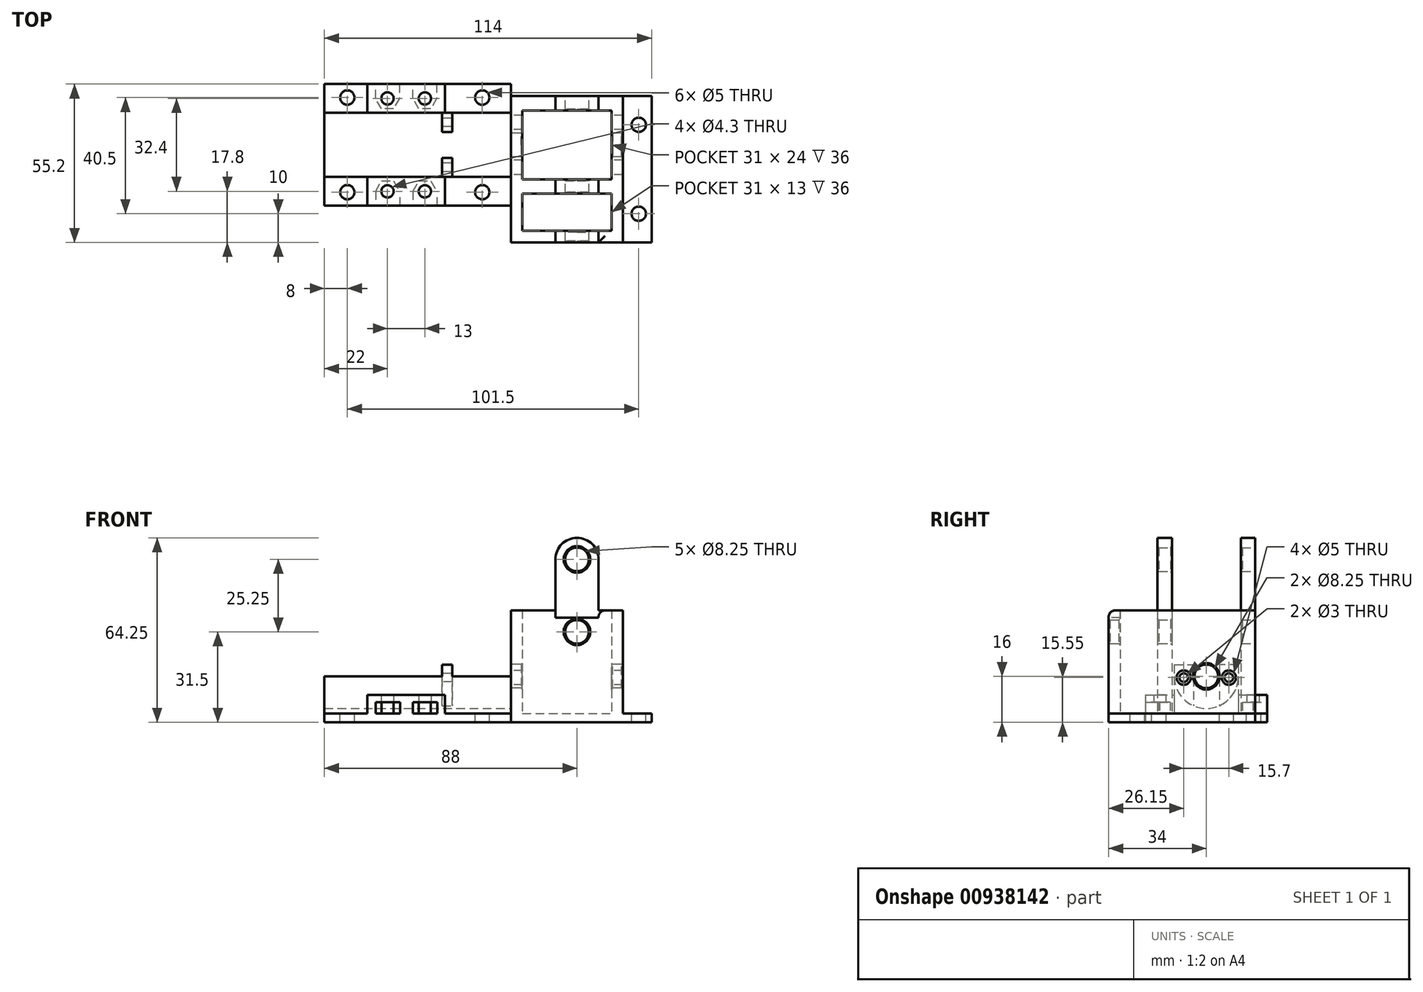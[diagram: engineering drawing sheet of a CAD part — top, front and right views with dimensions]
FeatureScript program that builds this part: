
annotation { "Feature Type Name" : "Feature", "Feature Type Description" : "" }
export const myFeature = defineFeature(function(context is Context, id is Id, definition is map)
    precondition{}
    {
        {
            var Q0;
            Q0=qCreatedBy(makeId("Top.planeOp"),FACE);
            var sketch = newSketch(context, id + "F0", { "sketchPlane" : qUnion([Q0])});
            skPoint(sketch, "E0.middle", {"position": v(0, 0) * mm});
            skLineSegment(sketch, "E1", {"start": v(0, 25.5) * mm, "end": v(0, -25.5) * mm});
            skLineSegment(sketch, "E2.bottom", {"start": v(0, 25.5) * mm, "end": v(39, 25.5) * mm});
            skLineSegment(sketch, "E2.right", {"start": v(39, 25.5) * mm, "end": v(39, -25.5) * mm});
            skLineSegment(sketch, "E3", {"start": v(4, 20.5) * mm, "end": v(35, 20.5) * mm});
            skLineSegment(sketch, "E4", {"start": v(0, -25.5) * mm, "end": v(39, -25.5) * mm});
            skLineSegment(sketch, "E5", {"start": v(4, 20.5) * mm, "end": v(4, -3.5) * mm});
            skLineSegment(sketch, "E6", {"start": v(35, 20.5) * mm, "end": v(35, -3.5) * mm});
            skLineSegment(sketch, "E7", {"start": v(35, -21.5) * mm, "end": v(4, -21.5) * mm});
            skLineSegment(sketch, "E8", {"start": v(23, 20.5) * mm, "end": v(23, -21.5) * mm, "construction": true});
            skLineSegment(sketch, "E9", {"start": v(4, -3.5) * mm, "end": v(35, -3.5) * mm});
            skLineSegment(sketch, "E10", {"start": v(4, -8.5) * mm, "end": v(35, -8.5) * mm});
            skLineSegment(sketch, "E11", {"start": v(35, -8.5) * mm, "end": v(35, -21.5) * mm});
            skLineSegment(sketch, "E12", {"start": v(4, -8.5) * mm, "end": v(4, -21.5) * mm});
            skLineSegment(sketch, "E13", {"start": v(39, 25.5) * mm, "end": v(49, 25.5) * mm});
            skLineSegment(sketch, "E14", {"start": v(49, 25.5) * mm, "end": v(49, -25.5) * mm});
            skLineSegment(sketch, "E15", {"start": v(49, -25.5) * mm, "end": v(39, -25.5) * mm});
            skCircle(sketch, "E16", {"center": v(44.5, 15.5) * mm, "radius": 2.5 * mm});
            skCircle(sketch, "E17", {"center": v(44.5, -15.5) * mm, "radius": 2.5 * mm});
            skLineSegment(sketch, "E18", {"start": v(44.5, 15.5) * mm, "end": v(44.5, -15.5) * mm, "construction": true});
            skPoint(sketch, "E19", {"position": v(44.5, 0) * mm});
            skPoint(sketch, "E20", {"position": v(49, 0) * mm});
            skSolve(sketch);
        }
        {
            var Q0;
            Q0=makeQuery(id+"F0.imprint","IMPRINT",FACE,{"disambiguationData":[TD([[makeQuery(id+"F0.imprint","IMPRINT",EDGE,{"derivedFrom":sQuery(id+"F0.wireOp",EDGE,"E3")}),-1.0]])]});
            var Q1;
            Q1=makeQuery(id+"F0.imprint","IMPRINT",FACE,{"disambiguationData":[TD([[makeQuery(id+"F0.imprint","IMPRINT",EDGE,{"derivedFrom":sQuery(id+"F0.wireOp",EDGE,"E7")}),-1.0]])]});
            var Q2;
            Q2=makeQuery(id+"F0.imprint","IMPRINT",FACE,{"disambiguationData":[TD([[makeQuery(id+"F0.imprint","IMPRINT",EDGE,{"derivedFrom":sQuery(id+"F0.wireOp",EDGE,"E2.right")}),1.0]])]});
            var Q3;
            Q3=makeQuery(id+"F0.imprint","IMPRINT",FACE,{"disambiguationData":[TD([[makeQuery(id+"F0.imprint","IMPRINT",EDGE,{"derivedFrom":sQuery(id+"F0.wireOp",EDGE,"E1")}),1.0]])]});
            extrude(context, id + "F1", {"entities" : qUnion([Q0, Q1, Q2, Q3]), "oppositeDirection" : true, "depth" : 3 * mm, "offsetDistance" : 25 * mm});
        }
        {
            var Q0;
            {var subQ0=sQuery(id+"F0.wireOp",EDGE,"E1");Q0=makeQuery(id+"F0.imprint","IMPRINT",FACE,{"disambiguationData":[TD([[makeQuery(id+"F0.imprint","IMPRINT",EDGE,{"derivedFrom":subQ0}),1.0]])]});}
            extrude(context, id + "F2", {"entities" : qUnion([Q0]), "operationType" : NewBodyOperationType.ADD, "depth" : 13 * mm + 15.5 * mm + 7.5 * mm, "offsetDistance" : 25 * mm});
        }
        {
            var Q0;
            Q0=makeQuery(id+"F2.opExtrude","SWEPT_FACE",FACE,{"disambiguationData":[OSD([sQuery(id+"F0.wireOp",EDGE,"E1")])]});
            var sketch = newSketch(context, id + "F3", { "sketchPlane" : qUnion([Q0])});
            skCircle(sketch, "E21", {"center": v(-8.5, 13) * mm, "radius": 4.12 * mm});
            skLineSegment(sketch, "E22", {"start": v(-19.7, -3) * mm, "end": v(2.7, -3) * mm});
            skArc(sketch, "E23", {"start": v(-19.7, 13) * mm, "mid": v(-8.5, 1.8) * mm, "end": v(2.7, 13) * mm});
            skLineSegment(sketch, "E24", {"start": v(-19.7, 13) * mm, "end": v(-19.7, -3) * mm});
            skLineSegment(sketch, "E25", {"start": v(2.7, 13) * mm, "end": v(2.7, -3) * mm});
            skPoint(sketch, "E26.orphan", {"position": v(-8.25, 36) * mm});
            skLineSegment(sketch, "E27", {"start": v(-8.5, 13) * mm, "end": v(-8.5, 22.2) * mm, "construction": true});
            skLineSegment(sketch, "E28", {"start": v(2.7, 0) * mm, "end": v(12.7, 0) * mm});
            skLineSegment(sketch, "E29", {"start": v(12.7, 0) * mm, "end": v(12.7, -3) * mm});
            skLineSegment(sketch, "E30", {"start": v(12.7, -3) * mm, "end": v(2.7, -3) * mm});
            skLineSegment(sketch, "E31", {"start": v(-19.7, 0) * mm, "end": v(-29.7, 0) * mm});
            skLineSegment(sketch, "E32", {"start": v(-29.7, 0) * mm, "end": v(-29.7, -3) * mm});
            skLineSegment(sketch, "E33", {"start": v(-29.7, -3) * mm, "end": v(-19.7, -3) * mm});
            skSolve(sketch);
        }
        {
            var Q0;
            Q0=makeQuery(id+"F3.imprint","IMPRINT",FACE,{"disambiguationData":[TD([[makeQuery(id+"F3.imprint","IMPRINT",EDGE,{"derivedFrom":sQuery(id+"F3.wireOp",EDGE,"E21")}),1.0]])]});
            extrude(context, id + "F4", {"entities" : qUnion([Q0]), "operationType" : NewBodyOperationType.REMOVE, "endBound" : BoundingType.THROUGH_ALL, "oppositeDirection" : true, "depth" : 3 * mm, "offsetDistance" : 25 * mm});
        }
        {
            var Q0;
            Q0=makeQuery(id+"F2.opExtrude","CAP_FACE",FACE,{"disambiguationData":[OSD([sQuery(id+"F0.wireOp",EDGE,"E1"),sQuery(id+"F0.wireOp",EDGE,"E2.bottom"),sQuery(id+"F0.wireOp",EDGE,"E2.top"),sQuery(id+"F0.wireOp",EDGE,"E2.right"),sQuery(id+"F0.wireOp",EDGE,"gcLeu1ae-8P9o-23Q4-LKgT-iucjTtS8KbHA"),sQuery(id+"F0.wireOp",EDGE,"E3"),sQuery(id+"F0.wireOp",EDGE,"sOh78GjP-uAya-5xBB-zDQr-sfzLusMJ1pns")])],"isStart":false});
            var sketch = newSketch(context, id + "F5", { "sketchPlane" : qUnion([Q0])});
            skLineSegment(sketch, "E34.bottom", {"start": v(30.5, 20.5) * mm, "end": v(15.5, 20.5) * mm});
            skLineSegment(sketch, "E34.top", {"start": v(30.5, 25.5) * mm, "end": v(15.5, 25.5) * mm});
            skLineSegment(sketch, "E34.left", {"start": v(30.5, 20.5) * mm, "end": v(30.5, 25.5) * mm});
            skLineSegment(sketch, "E34.right", {"start": v(15.5, 20.5) * mm, "end": v(15.5, 25.5) * mm});
            skPoint(sketch, "E35", {"position": v(23, 20.5) * mm});
            skLineSegment(sketch, "E36.bottom", {"start": v(15.5, -3.5) * mm, "end": v(30.5, -3.5) * mm});
            skLineSegment(sketch, "E36.top", {"start": v(15.5, -8.5) * mm, "end": v(30.5, -8.5) * mm});
            skLineSegment(sketch, "E36.left", {"start": v(15.5, -3.5) * mm, "end": v(15.5, -8.5) * mm});
            skLineSegment(sketch, "E36.right", {"start": v(30.5, -3.5) * mm, "end": v(30.5, -8.5) * mm});
            skLineSegment(sketch, "E37.bottom", {"start": v(30.5, -21.5) * mm, "end": v(15.5, -21.5) * mm});
            skLineSegment(sketch, "E37.top", {"start": v(30.5, -25.5) * mm, "end": v(15.5, -25.5) * mm});
            skLineSegment(sketch, "E37.left", {"start": v(15.5, -21.5) * mm, "end": v(15.5, -25.5) * mm});
            skLineSegment(sketch, "E37.right", {"start": v(30.5, -21.5) * mm, "end": v(30.5, -25.5) * mm});
            skSolve(sketch);
        }
        {
            var Q0;
            Q0=makeQuery(id+"F5.imprint","IMPRINT",FACE,{"disambiguationData":[TD([[makeQuery(id+"F5.imprint","IMPRINT",EDGE,{"derivedFrom":sQuery(id+"F5.wireOp",EDGE,"E34.bottom")}),1.0]])]});
            var Q1;
            Q1=makeQuery(id+"F5.imprint","IMPRINT",FACE,{"disambiguationData":[TD([[makeQuery(id+"F5.imprint","IMPRINT",EDGE,{"derivedFrom":sQuery(id+"F5.wireOp",EDGE,"MIDvq16X-2qJM-DpOX-ttxi-7ILKl5nktbrk.bottom")}),1.0]])]});
            var Q2;
            {var subQ0=sQuery(id+"F5.wireOp",EDGE,"MIDvq16X-2qJM-DpOX-ttxi-7ILKl5nktbrk.top");Q2=makeQuery(id+"F5.imprint","IMPRINT",FACE,{"disambiguationData":[TD([[makeQuery(id+"F5.imprint","IMPRINT",EDGE,{"derivedFrom":subQ0}),1.0]])]});}
            var Q3;
            Q3=makeQuery(id+"F5.imprint","IMPRINT",FACE,{"disambiguationData":[TD([[makeQuery(id+"F5.imprint","IMPRINT",EDGE,{"derivedFrom":sQuery(id+"F5.wireOp",EDGE,"E36.bottom")}),-1.0]])]});
            extrude(context, id + "F6", {"entities" : qUnion([Q0, Q1, Q2, Q3]), "operationType" : NewBodyOperationType.ADD, "depth" : 25.25 * mm, "offsetDistance" : 25 * mm});
        }
        {
            var Q0;
            {var subQ0=sQuery(id+"F0.wireOp",EDGE,"E2.bottom");Q0=makeQuery(id+"F6.boolean.opBoolean","MERGE",FACE,{"derivedFrom":[makeQuery(id+"F2.boolean.opBoolean","MERGE",FACE,{"derivedFrom":[makeQuery(id+"F1.opExtrude","SWEPT_FACE",FACE,{"disambiguationData":[OSD([subQ0])]}),makeQuery(id+"F2.opExtrude","SWEPT_FACE",FACE,{"disambiguationData":[OSD([subQ0])]})]}),makeQuery(id+"F6.opExtrude","SWEPT_FACE",FACE,{"disambiguationData":[OSD([sQuery(id+"F5.wireOp",EDGE,"hZvgbcKE-K8w2-tHia-kABx-2Idw38wRMYFB.top")])]})]});}
            var sketch = newSketch(context, id + "F7", { "sketchPlane" : qUnion([Q0])});
            skCircle(sketch, "E38", {"center": v(-23, 28.5) * mm, "radius": 4.12 * mm});
            skCircle(sketch, "E39", {"center": v(-23, 53.75) * mm, "radius": 4.12 * mm});
            skSolve(sketch);
        }
        {
            var Q0;
            {var subQ0=sQuery(id+"F7.wireOp",EDGE,"E38");var subQ1=sQuery(id+"F5.wireOp",EDGE,"sYnbmEzX-ozCD-b1SQ-Veyi-UDucfDWyLtHq.right");var subQ2=sQuery(id+"F5.wireOp",EDGE,"sYnbmEzX-ozCD-b1SQ-Veyi-UDucfDWyLtHq.bottom");var subQ3=sQuery(id+"F0.wireOp",EDGE,"E2.bottom");var subQ4=makeQuery(id+"FMjW4kx9HAlJB9q_1.opExtrude","SWEPT_EDGE",EDGE,{"disambiguationData":[OSD([subQ3,subQ2,subQ1])]});var subQ5=makeQuery(id+"F7.imprint","INTERSECT",VERTEX,{"derivedFrom":[subQ4,subQ0]});Q0=makeQuery(id+"F7.imprint","IMPRINT",FACE,{"disambiguationData":[TD([[makeQuery(id+"F7.imprint","IMPRINT",EDGE,{"disambiguationData":[TD([[subQ5,1.0]])],"derivedFrom":subQ0}),1.0]])]});}
            var Q1;
            Q1=makeQuery(id+"F7.imprint","IMPRINT",FACE,{"disambiguationData":[TD([[makeQuery(id+"F7.imprint","IMPRINT",EDGE,{"derivedFrom":sQuery(id+"F7.wireOp",EDGE,"E39")}),1.0]])]});
            extrude(context, id + "F8", {"entities" : qUnion([Q0, Q1]), "operationType" : NewBodyOperationType.REMOVE, "endBound" : BoundingType.THROUGH_ALL, "oppositeDirection" : true, "depth" : 25 * mm, "offsetDistance" : 25 * mm});
        }
        {
            var Q0;
            Q0=makeQuery(id+"F3.imprint","IMPRINT",FACE,{"disambiguationData":[TD([[makeQuery(id+"F3.imprint","IMPRINT",EDGE,{"derivedFrom":sQuery(id+"F3.wireOp",EDGE,"E22")}),1.0]])]});
            var Q1;
            {var subQ2=sQuery(id+"F3.wireOp",EDGE,"E28");Q1=makeQuery(id+"F3.imprint","IMPRINT",FACE,{"disambiguationData":[TD([[makeQuery(id+"F3.imprint","IMPRINT",EDGE,{"derivedFrom":subQ2}),-1.0]])]});}
            var Q2;
            {var subQ1=sQuery(id+"F3.wireOp",EDGE,"E24");var subQ3=sQuery(id+"F3.wireOp",EDGE,"E31");var subQ4=makeQuery(id+"F3.imprint","INTERSECT",VERTEX,{"derivedFrom":[subQ1,subQ3]});Q2=makeQuery(id+"F3.imprint","IMPRINT",FACE,{"disambiguationData":[TD([[makeQuery(id+"F3.imprint","IMPRINT",EDGE,{"disambiguationData":[TD([[subQ4,-1.0]])],"derivedFrom":subQ1}),-1.0]])]});}
            var Q3;
            {var subQ0=sQuery(id+"F3.wireOp",EDGE,"E32");Q3=makeQuery(id+"F3.imprint","IMPRINT",FACE,{"disambiguationData":[TD([[makeQuery(id+"F3.imprint","IMPRINT",EDGE,{"derivedFrom":subQ0}),1.0]])]});}
            extrude(context, id + "F9", {"entities" : qUnion([Q0, Q1, Q2, Q3]), "operationType" : NewBodyOperationType.ADD, "depth" : 65 * mm, "offsetDistance" : 25 * mm});
        }
        {
            var Q0;
            Q0=makeQuery(id+"F9.boolean.opBoolean","MERGE",FACE,{"derivedFrom":[makeQuery(id+"F1.opExtrude","CAP_FACE",FACE,{"disambiguationData":[OSD([sQuery(id+"F0.wireOp",EDGE,"E1"),sQuery(id+"F0.wireOp",EDGE,"E2.bottom"),sQuery(id+"F0.wireOp",EDGE,"E2.right"),sQuery(id+"F0.wireOp",EDGE,"E4")])],"isStart":false}),makeQuery(id+"F9.opExtrude","SWEPT_FACE",FACE,{"disambiguationData":[OSD([sQuery(id+"F3.wireOp",EDGE,"E22")])]})]});
            var sketch = newSketch(context, id + "F10", { "sketchPlane" : qUnion([Q0])});
            skLineSegment(sketch, "E40.bottom", {"start": v(-24, 2.7) * mm, "end": v(-20.5, 2.7) * mm});
            skLineSegment(sketch, "E40.top", {"start": v(-24, -4) * mm, "end": v(-20.5, -4) * mm});
            skLineSegment(sketch, "E40.left", {"start": v(-24, 2.7) * mm, "end": v(-24, -4) * mm});
            skLineSegment(sketch, "E40.right", {"start": v(-20.5, 2.7) * mm, "end": v(-20.5, -4) * mm});
            skLineSegment(sketch, "E41.bottom", {"start": v(-20.5, -19.7) * mm, "end": v(-24, -19.7) * mm});
            skLineSegment(sketch, "E41.top", {"start": v(-20.5, -13) * mm, "end": v(-24, -13) * mm});
            skLineSegment(sketch, "E41.left", {"start": v(-20.5, -19.7) * mm, "end": v(-20.5, -13) * mm});
            skLineSegment(sketch, "E41.right", {"start": v(-24, -19.7) * mm, "end": v(-24, -13) * mm});
            skPoint(sketch, "E42", {"position": v(0, -8.5) * mm});
            skSolve(sketch);
        }
        {
            var Q0;
            Q0=makeQuery(id+"F10.imprint","IMPRINT",FACE,{"disambiguationData":[TD([[makeQuery(id+"F10.imprint","IMPRINT",EDGE,{"derivedFrom":sQuery(id+"F10.wireOp",EDGE,"1N8PbtRb-MMLw-GFMX-CoVd-qPCvI8zf9gy1")}),1.0]])]});
            var Q1;
            Q1=makeQuery(id+"F10.imprint","IMPRINT",FACE,{"disambiguationData":[TD([[makeQuery(id+"F10.imprint","IMPRINT",EDGE,{"derivedFrom":sQuery(id+"F10.wireOp",EDGE,"qHMIfVYf-9KHw-zTNj-7CN8-sHAUkWgPVhBX")}),-1.0]])]});
            var Q2;
            Q2=makeQuery(id+"F10.imprint","IMPRINT",FACE,{"disambiguationData":[TD([[makeQuery(id+"F10.imprint","IMPRINT",EDGE,{"derivedFrom":sQuery(id+"F10.wireOp",EDGE,"E40.bottom")}),-1.0]])]});
            var Q3;
            Q3=makeQuery(id+"F10.imprint","IMPRINT",FACE,{"disambiguationData":[TD([[makeQuery(id+"F10.imprint","IMPRINT",EDGE,{"derivedFrom":sQuery(id+"F10.wireOp",EDGE,"E41.bottom")}),-1.0]])]});
            extrude(context, id + "F11", {"entities" : qUnion([Q0, Q1, Q2, Q3]), "operationType" : NewBodyOperationType.ADD, "flatOperationType" : FlatOperationType.REMOVE, "oppositeDirection" : true, "depth" : 5 * mm + 15 * mm, "offsetDistance" : 25 * mm, "domain" : OperationDomain.MODEL});
        }
        {
            var Q0;
            Q0=makeQuery(id+"F11.opExtrude","SWEPT_FACE",FACE,{"disambiguationData":[OSD([sQuery(id+"F10.wireOp",EDGE,"E41.right")])]});
            var sketch = newSketch(context, id + "F12", { "sketchPlane" : qUnion([Q0])});
            skCircle(sketch, "E43", {"center": v(-16.35, 12.55) * mm, "radius": 1.5 * mm});
            skCircle(sketch, "E44", {"center": v(-0.65, 12.55) * mm, "radius": 1.5 * mm});
            skSolve(sketch);
        }
        {
            var Q0;
            Q0=makeQuery(id+"F12.imprint","IMPRINT",FACE,{"disambiguationData":[TD([[makeQuery(id+"F12.imprint","IMPRINT",EDGE,{"derivedFrom":sQuery(id+"F12.wireOp",EDGE,"E43")}),1.0]])]});
            var Q1;
            Q1=makeQuery(id+"F12.imprint","IMPRINT",FACE,{"disambiguationData":[TD([[makeQuery(id+"F12.imprint","IMPRINT",EDGE,{"derivedFrom":sQuery(id+"F12.wireOp",EDGE,"E44")}),1.0]])]});
            extrude(context, id + "F13", {"entities" : qUnion([Q0, Q1]), "operationType" : NewBodyOperationType.REMOVE, "oppositeDirection" : true, "depth" : 4 * mm, "offsetDistance" : 25 * mm});
        }
        {
            var Q0;
            Q0=makeQuery(id+"F5.imprint","IMPRINT",FACE,{"disambiguationData":[TD([[makeQuery(id+"F5.imprint","IMPRINT",EDGE,{"derivedFrom":sQuery(id+"F5.wireOp",EDGE,"E37.bottom")}),1.0]])]});
            extrude(context, id + "F14", {"entities" : qUnion([Q0]), "operationType" : NewBodyOperationType.REMOVE, "oppositeDirection" : true, "depth" : 2.5 * mm, "offsetDistance" : 25 * mm});
        }
        {
            var Q0;
            Q0=makeQuery(id+"F9.opExtrude","SWEPT_FACE",FACE,{"disambiguationData":[OSD([sQuery(id+"F3.wireOp",EDGE,"E28")])]});
            var sketch = newSketch(context, id + "F15", { "sketchPlane" : qUnion([Q0])});
            skCircle(sketch, "E45", {"center": v(-10, -8) * mm, "radius": 2.5 * mm});
            skPoint(sketch, "E45.centerSnap0", {"position": v(0, -7.7) * mm});
            skCircle(sketch, "E46", {"center": v(-57, -8) * mm, "radius": 2.5 * mm});
            skCircle(sketch, "E47", {"center": v(-30, -7.7) * mm, "radius": 2.15 * mm});
            skCircle(sketch, "E48", {"center": v(-43, -7.7) * mm, "radius": 2.15 * mm});
            skCircle(sketch, "E49", {"center": v(-30, 24.7) * mm, "radius": 2.15 * mm});
            skCircle(sketch, "E50", {"center": v(-43, 24.7) * mm, "radius": 2.15 * mm});
            skCircle(sketch, "E51.cCircle", {"center": v(-30, -7.7) * mm, "radius": 3.6 * mm, "construction": true});
            skLineSegment(sketch, "E51.0", {"start": v(-32.08, -4.1) * mm, "end": v(-27.92, -4.1) * mm});
            skLineSegment(sketch, "E51.1", {"start": v(-27.92, -4.1) * mm, "end": v(-25.62, -8.1) * mm});
            skLineSegment(sketch, "E51.5", {"start": v(-34.16, -7.7) * mm, "end": v(-32.08, -4.1) * mm});
            skPoint(sketch, "E51.0.midPoint", {"position": v(-30, -4.1) * mm});
            skCircle(sketch, "E52.cCircle", {"center": v(-43, -7.7) * mm, "radius": 3.6 * mm, "construction": true});
            skLineSegment(sketch, "E52.0", {"start": v(-47.16, -7.7) * mm, "end": v(-45.08, -4.1) * mm});
            skLineSegment(sketch, "E52.1", {"start": v(-45.08, -4.1) * mm, "end": v(-40.92, -4.1) * mm});
            skLineSegment(sketch, "E52.2", {"start": v(-40.92, -4.1) * mm, "end": v(-38.62, -8.1) * mm});
            skPoint(sketch, "E52.0.midPoint", {"position": v(-46.12, -5.9) * mm});
            skCircle(sketch, "E53.cCircle", {"center": v(-43, 24.7) * mm, "radius": 3.6 * mm, "construction": true});
            skLineSegment(sketch, "E53.3", {"start": v(-38.84, 24.7) * mm, "end": v(-40.92, 21.1) * mm});
            skLineSegment(sketch, "E53.4", {"start": v(-40.92, 21.1) * mm, "end": v(-45.08, 21.1) * mm});
            skLineSegment(sketch, "E53.5", {"start": v(-45.08, 21.1) * mm, "end": v(-47.16, 24.7) * mm});
            skCircle(sketch, "E54.cCircle", {"center": v(-30, 24.7) * mm, "radius": 3.6 * mm, "construction": true});
            skLineSegment(sketch, "E54.2", {"start": v(-25.84, 24.7) * mm, "end": v(-27.92, 21.1) * mm});
            skLineSegment(sketch, "E54.3", {"start": v(-27.92, 21.1) * mm, "end": v(-32.08, 21.1) * mm});
            skLineSegment(sketch, "E54.4", {"start": v(-32.08, 21.1) * mm, "end": v(-34.16, 24.7) * mm});
            skLineSegment(sketch, "E55", {"start": v(-47.16, -7.7) * mm, "end": v(-47.16, -12.7) * mm});
            skLineSegment(sketch, "E56", {"start": v(-47.16, -12.7) * mm, "end": v(-38.62, -12.7) * mm});
            skLineSegment(sketch, "E57", {"start": v(-38.62, -12.7) * mm, "end": v(-38.62, -8.1) * mm});
            skLineSegment(sketch, "E58", {"start": v(-34.16, -7.7) * mm, "end": v(-34.16, -12.7) * mm});
            skLineSegment(sketch, "E59", {"start": v(-34.16, -12.7) * mm, "end": v(-25.62, -12.7) * mm});
            skLineSegment(sketch, "E60", {"start": v(-25.62, -12.7) * mm, "end": v(-25.62, -8.1) * mm});
            skLineSegment(sketch, "E61", {"start": v(-47.16, 24.7) * mm, "end": v(-47.16, 29.7) * mm});
            skLineSegment(sketch, "E62", {"start": v(-47.16, 29.7) * mm, "end": v(-38.84, 29.7) * mm});
            skLineSegment(sketch, "E63", {"start": v(-38.84, 29.7) * mm, "end": v(-38.84, 24.7) * mm});
            skLineSegment(sketch, "E64", {"start": v(-34.16, 24.7) * mm, "end": v(-34.16, 29.7) * mm});
            skLineSegment(sketch, "E65", {"start": v(-34.16, 29.7) * mm, "end": v(-25.84, 29.7) * mm});
            skLineSegment(sketch, "E66", {"start": v(-25.84, 29.7) * mm, "end": v(-25.84, 24.7) * mm});
            skLineSegment(sketch, "E67", {"start": v(-47.16, -12.7) * mm, "end": v(-50, -12.7) * mm});
            skLineSegment(sketch, "E68", {"start": v(-50, -12.7) * mm, "end": v(-50, -2.7) * mm});
            skLineSegment(sketch, "E69", {"start": v(-23, -2.7) * mm, "end": v(-23, -12.7) * mm});
            skLineSegment(sketch, "E70", {"start": v(-23, -12.7) * mm, "end": v(-25.62, -12.7) * mm});
            skLineSegment(sketch, "E71", {"start": v(-38.62, -12.7) * mm, "end": v(-34.16, -12.7) * mm});
            skLineSegment(sketch, "E72", {"start": v(-50, 19.7) * mm, "end": v(-50, 29.7) * mm});
            skLineSegment(sketch, "E73", {"start": v(-50, 29.7) * mm, "end": v(-47.16, 29.7) * mm});
            skLineSegment(sketch, "E74", {"start": v(-38.84, 29.7) * mm, "end": v(-34.16, 29.7) * mm});
            skLineSegment(sketch, "E75", {"start": v(-25.84, 29.7) * mm, "end": v(-23, 29.7) * mm});
            skLineSegment(sketch, "E76", {"start": v(-23, 29.7) * mm, "end": v(-23, 19.7) * mm});
            skLineSegment(sketch, "E77", {"start": v(-23, 19.7) * mm, "end": v(-50, 19.7) * mm});
            skCircle(sketch, "E78", {"center": v(-10, 25) * mm, "radius": 2.5 * mm});
            skCircle(sketch, "E79", {"center": v(-57, 25) * mm, "radius": 2.5 * mm});
            skLineSegment(sketch, "E80", {"start": v(-23, -7.7) * mm, "end": v(-30, -7.7) * mm, "construction": true});
            skLineSegment(sketch, "E81", {"start": v(-43, -7.7) * mm, "end": v(-50, -7.7) * mm, "construction": true});
            skLineSegment(sketch, "E82", {"start": v(-23, -2.7) * mm, "end": v(-50, -2.7) * mm});
            skLineSegment(sketch, "E83", {"start": v(-10, 25) * mm, "end": v(-10, -8) * mm, "construction": true});
            skPoint(sketch, "E84", {"position": v(-10, 8.5) * mm});
            skSolve(sketch);
        }
        {
            var Q0;
            Q0=makeQuery(id+"F15.imprint","IMPRINT",FACE,{"disambiguationData":[TD([[makeQuery(id+"F15.imprint","IMPRINT",EDGE,{"derivedFrom":sQuery(id+"F15.wireOp",EDGE,"E46")}),1.0]])]});
            var Q1;
            Q1=makeQuery(id+"F15.imprint","IMPRINT",FACE,{"disambiguationData":[TD([[makeQuery(id+"F15.imprint","IMPRINT",EDGE,{"derivedFrom":sQuery(id+"F15.wireOp",EDGE,"E45")}),1.0]])]});
            var Q2;
            Q2=makeQuery(id+"F15.imprint","IMPRINT",FACE,{"disambiguationData":[TD([[makeQuery(id+"F15.imprint","IMPRINT",EDGE,{"derivedFrom":sQuery(id+"F15.wireOp",EDGE,"E78")}),1.0]])]});
            var Q3;
            Q3=makeQuery(id+"F15.imprint","IMPRINT",FACE,{"disambiguationData":[TD([[makeQuery(id+"F15.imprint","IMPRINT",EDGE,{"derivedFrom":sQuery(id+"F15.wireOp",EDGE,"E79")}),1.0]])]});
            extrude(context, id + "F16", {"entities" : qUnion([Q0, Q1, Q2, Q3]), "operationType" : NewBodyOperationType.REMOVE, "endBound" : BoundingType.THROUGH_ALL, "oppositeDirection" : true, "depth" : 25 * mm, "offsetDistance" : 25 * mm});
        }
        {
            var Q0;
            Q0=makeQuery(id+"F15.imprint","IMPRINT",FACE,{"disambiguationData":[TD([[makeQuery(id+"F15.imprint","IMPRINT",EDGE,{"derivedFrom":sQuery(id+"F15.wireOp",EDGE,"E51.0")}),1.0]])]});
            var Q1;
            Q1=makeQuery(id+"F15.imprint","IMPRINT",FACE,{"disambiguationData":[TD([[makeQuery(id+"F15.imprint","IMPRINT",EDGE,{"derivedFrom":sQuery(id+"F15.wireOp",EDGE,"E53.3")}),1.0]])]});
            var Q2;
            Q2=makeQuery(id+"F15.imprint","IMPRINT",FACE,{"disambiguationData":[TD([[makeQuery(id+"F15.imprint","IMPRINT",EDGE,{"derivedFrom":sQuery(id+"F15.wireOp",EDGE,"E48")}),-1.0]])]});
            var Q3;
            Q3=makeQuery(id+"F15.imprint","IMPRINT",FACE,{"disambiguationData":[TD([[makeQuery(id+"F15.imprint","IMPRINT",EDGE,{"derivedFrom":sQuery(id+"F15.wireOp",EDGE,"E47")}),-1.0]])]});
            var Q4;
            Q4=makeQuery(id+"F15.imprint","IMPRINT",FACE,{"disambiguationData":[TD([[makeQuery(id+"F15.imprint","IMPRINT",EDGE,{"derivedFrom":sQuery(id+"F15.wireOp",EDGE,"E50")}),-1.0]])]});
            var Q5;
            Q5=makeQuery(id+"F15.imprint","IMPRINT",FACE,{"disambiguationData":[TD([[makeQuery(id+"F15.imprint","IMPRINT",EDGE,{"derivedFrom":sQuery(id+"F15.wireOp",EDGE,"E49")}),-1.0]])]});
            extrude(context, id + "F17", {"entities" : qUnion([Q0, Q1, Q2, Q3, Q4, Q5]), "operationType" : NewBodyOperationType.ADD, "depth" : 4 * mm + 2.5 * mm, "offsetDistance" : 25 * mm});
        }
        {
            var Q0;
            Q0=makeQuery(id+"F15.imprint","IMPRINT",FACE,{"disambiguationData":[TD([[makeQuery(id+"F15.imprint","IMPRINT",EDGE,{"derivedFrom":sQuery(id+"F15.wireOp",EDGE,"E48")}),-1.0]])]});
            var Q1;
            Q1=makeQuery(id+"F15.imprint","IMPRINT",FACE,{"disambiguationData":[TD([[makeQuery(id+"F15.imprint","IMPRINT",EDGE,{"derivedFrom":sQuery(id+"F15.wireOp",EDGE,"E47")}),-1.0]])]});
            var Q2;
            Q2=makeQuery(id+"F15.imprint","IMPRINT",FACE,{"disambiguationData":[TD([[makeQuery(id+"F15.imprint","IMPRINT",EDGE,{"derivedFrom":sQuery(id+"F15.wireOp",EDGE,"E50")}),-1.0]])]});
            var Q3;
            Q3=makeQuery(id+"F15.imprint","IMPRINT",FACE,{"disambiguationData":[TD([[makeQuery(id+"F15.imprint","IMPRINT",EDGE,{"derivedFrom":sQuery(id+"F15.wireOp",EDGE,"E49")}),-1.0]])]});
            extrude(context, id + "F18", {"entities" : qUnion([Q0, Q1, Q2, Q3]), "operationType" : NewBodyOperationType.REMOVE, "depth" : 4 * mm, "offsetDistance" : 25 * mm});
        }
        {
            var Q0;
            Q0=makeQuery(id+"F11.opExtrude","SWEPT_FACE",FACE,{"disambiguationData":[OSD([sQuery(id+"F10.wireOp",EDGE,"E41.left")])]});
            var sketch = newSketch(context, id + "F19", { "sketchPlane" : qUnion([Q0])});
            skCircle(sketch, "E85", {"center": v(16.35, 12.55) * mm, "radius": 2.5 * mm});
            skCircle(sketch, "E86", {"center": v(0.65, 12.55) * mm, "radius": 2.5 * mm});
            skSolve(sketch);
        }
        {
            var Q0;
            Q0=makeQuery(id+"F19.imprint","IMPRINT",FACE,{"disambiguationData":[TD([[makeQuery(id+"F19.imprint","IMPRINT",EDGE,{"derivedFrom":sQuery(id+"F19.wireOp",EDGE,"E86")}),1.0]])]});
            var Q1;
            Q1=makeQuery(id+"F19.imprint","IMPRINT",FACE,{"disambiguationData":[TD([[makeQuery(id+"F19.imprint","IMPRINT",EDGE,{"derivedFrom":sQuery(id+"F19.wireOp",EDGE,"E85")}),1.0]])]});
            var Q2;
            Q2=makeQuery(id+"F19.imprint","IMPRINT",FACE,{"disambiguationData":[TD([[makeQuery(id+"F19.imprint","IMPRINT",EDGE,{"derivedFrom":makeQuery(id+"F13.boolean.opBoolean","INTERSECT",EDGE,{"derivedFrom":[makeQuery(id+"F11.opExtrude","SWEPT_FACE",FACE,{"disambiguationData":[OSD([sQuery(id+"F10.wireOp",EDGE,"E41.left")])]}),makeQuery(id+"F13.opExtrude","SWEPT_FACE",FACE,{"disambiguationData":[OSD([sQuery(id+"F12.wireOp",EDGE,"E43")])]})]})}),1.0]])]});
            extrude(context, id + "F20", {"entities" : qUnion([Q0, Q1, Q2]), "operationType" : NewBodyOperationType.REMOVE, "endBound" : BoundingType.THROUGH_ALL, "depth" : 25 * mm, "offsetDistance" : 25 * mm});
        }
        {
            var Q0;
            Q0=makeQuery(id+"F8.boolean.opBoolean","INTERSECT",EDGE,{"derivedFrom":[makeQuery(id+"F6.boolean.opBoolean","MERGE",FACE,{"derivedFrom":[makeQuery(id+"F2.opExtrude","SWEPT_FACE",FACE,{"disambiguationData":[OSD([sQuery(id+"F0.wireOp",EDGE,"E10")])]}),makeQuery(id+"F6.opExtrude","SWEPT_FACE",FACE,{"disambiguationData":[OSD([sQuery(id+"F5.wireOp",EDGE,"E36.top")])]})]}),makeQuery(id+"F8.opExtrude","SWEPT_FACE",FACE,{"disambiguationData":[OSD([sQuery(id+"F7.wireOp",EDGE,"E38")])]})]});
            var Q1;
            Q1=makeQuery(id+"F4.boolean.opBoolean","INTERSECT",EDGE,{"derivedFrom":[makeQuery(id+"F2.opExtrude","SWEPT_FACE",FACE,{"disambiguationData":[OSD([sQuery(id+"F0.wireOp",EDGE,"E2.right")])]}),makeQuery(id+"F4.opExtrude","SWEPT_FACE",FACE,{"disambiguationData":[OSD([sQuery(id+"F3.wireOp",EDGE,"E21")])]})]});
            var Q2;
            Q2=makeQuery(id+"F8.boolean.opBoolean","INTERSECT",EDGE,{"derivedFrom":[makeQuery(id+"F6.boolean.opBoolean","MERGE",FACE,{"derivedFrom":[makeQuery(id+"F2.opExtrude","SWEPT_FACE",FACE,{"disambiguationData":[OSD([sQuery(id+"F0.wireOp",EDGE,"E3")])]}),makeQuery(id+"F6.opExtrude","SWEPT_FACE",FACE,{"disambiguationData":[OSD([sQuery(id+"F5.wireOp",EDGE,"E34.bottom")])]})]}),makeQuery(id+"F8.opExtrude","SWEPT_FACE",FACE,{"disambiguationData":[OSD([sQuery(id+"F7.wireOp",EDGE,"E38")])]})]});
            var Q3;
            Q3=makeQuery(id+"F4.boolean.opBoolean","INTERSECT",EDGE,{"derivedFrom":[makeQuery(id+"F2.opExtrude","SWEPT_FACE",FACE,{"disambiguationData":[OSD([sQuery(id+"F0.wireOp",EDGE,"E5")])]}),makeQuery(id+"F4.opExtrude","SWEPT_FACE",FACE,{"disambiguationData":[OSD([sQuery(id+"F3.wireOp",EDGE,"E21")])]})]});
            var Q4;
            Q4=makeQuery(id+"F8.boolean.opBoolean","INTERSECT",EDGE,{"derivedFrom":[makeQuery(id+"F6.boolean.opBoolean","MERGE",FACE,{"derivedFrom":[makeQuery(id+"F2.opExtrude","SWEPT_FACE",FACE,{"disambiguationData":[OSD([sQuery(id+"F0.wireOp",EDGE,"E9")])]}),makeQuery(id+"F6.opExtrude","SWEPT_FACE",FACE,{"disambiguationData":[OSD([sQuery(id+"F5.wireOp",EDGE,"E36.bottom")])]})]}),makeQuery(id+"F8.opExtrude","SWEPT_FACE",FACE,{"disambiguationData":[OSD([sQuery(id+"F7.wireOp",EDGE,"E38")])]})]});
            var Q5;
            Q5=makeQuery(id+"F8.boolean.opBoolean","INTERSECT",EDGE,{"derivedFrom":[makeQuery(id+"F6.boolean.opBoolean","MERGE",FACE,{"derivedFrom":[makeQuery(id+"F2.opExtrude","SWEPT_FACE",FACE,{"disambiguationData":[OSD([sQuery(id+"F0.wireOp",EDGE,"E9")])]}),makeQuery(id+"F6.opExtrude","SWEPT_FACE",FACE,{"disambiguationData":[OSD([sQuery(id+"F5.wireOp",EDGE,"E36.bottom")])]})]}),makeQuery(id+"F8.opExtrude","SWEPT_FACE",FACE,{"disambiguationData":[OSD([sQuery(id+"F7.wireOp",EDGE,"E39")])]})]});
            var Q6;
            Q6=makeQuery(id+"F8.boolean.opBoolean","INTERSECT",EDGE,{"derivedFrom":[makeQuery(id+"F2.opExtrude","SWEPT_FACE",FACE,{"disambiguationData":[OSD([sQuery(id+"F0.wireOp",EDGE,"E7")])]}),makeQuery(id+"F8.opExtrude","SWEPT_FACE",FACE,{"disambiguationData":[OSD([sQuery(id+"F7.wireOp",EDGE,"E38")])]})]});
            var Q7;
            Q7=makeQuery(id+"F8.boolean.opBoolean","COPY",EDGE,{"derivedFrom":makeQuery(id+"F8.opExtrude","CAP_EDGE",EDGE,{"disambiguationData":[OSD([sQuery(id+"F7.wireOp",EDGE,"E39")])],"isStart":true})});
            var Q8;
            Q8=makeQuery(id+"F8.boolean.opBoolean","COPY",EDGE,{"derivedFrom":makeQuery(id+"F8.opExtrude","CAP_EDGE",EDGE,{"disambiguationData":[OSD([sQuery(id+"F7.wireOp",EDGE,"E38")])],"isStart":true})});
            var Q9;
            Q9=makeQuery(id+"F8.boolean.opBoolean","INTERSECT",EDGE,{"derivedFrom":[makeQuery(id+"F6.boolean.opBoolean","MERGE",FACE,{"derivedFrom":[makeQuery(id+"F2.opExtrude","SWEPT_FACE",FACE,{"disambiguationData":[OSD([sQuery(id+"F0.wireOp",EDGE,"E10")])]}),makeQuery(id+"F6.opExtrude","SWEPT_FACE",FACE,{"disambiguationData":[OSD([sQuery(id+"F5.wireOp",EDGE,"E36.top")])]})]}),makeQuery(id+"F8.opExtrude","SWEPT_FACE",FACE,{"disambiguationData":[OSD([sQuery(id+"F7.wireOp",EDGE,"E39")])]})]});
            var Q10;
            Q10=makeQuery(id+"F8.boolean.opBoolean","INTERSECT",EDGE,{"derivedFrom":[makeQuery(id+"F6.boolean.opBoolean","MERGE",FACE,{"derivedFrom":[makeQuery(id+"F2.opExtrude","SWEPT_FACE",FACE,{"disambiguationData":[OSD([sQuery(id+"F0.wireOp",EDGE,"E3")])]}),makeQuery(id+"F6.opExtrude","SWEPT_FACE",FACE,{"disambiguationData":[OSD([sQuery(id+"F5.wireOp",EDGE,"E34.bottom")])]})]}),makeQuery(id+"F8.opExtrude","SWEPT_FACE",FACE,{"disambiguationData":[OSD([sQuery(id+"F7.wireOp",EDGE,"E39")])]})]});
            var Q11;
            Q11=makeQuery(id+"F4.boolean.opBoolean","COPY",EDGE,{"derivedFrom":makeQuery(id+"F4.opExtrude","CAP_EDGE",EDGE,{"disambiguationData":[OSD([sQuery(id+"F3.wireOp",EDGE,"E21")])],"isStart":true})});
            var Q12;
            Q12=makeQuery(id+"F4.boolean.opBoolean","INTERSECT",EDGE,{"derivedFrom":[makeQuery(id+"F2.opExtrude","SWEPT_FACE",FACE,{"disambiguationData":[OSD([sQuery(id+"F0.wireOp",EDGE,"E6")])]}),makeQuery(id+"F4.opExtrude","SWEPT_FACE",FACE,{"disambiguationData":[OSD([sQuery(id+"F3.wireOp",EDGE,"E21")])]})]});
            var Q13;
            {var subQ0=sQuery(id+"F0.wireOp",EDGE,"E4");Q13=makeQuery(id+"F8.boolean.opBoolean","INTERSECT",EDGE,{"derivedFrom":[makeQuery(id+"F2.boolean.opBoolean","MERGE",FACE,{"derivedFrom":[makeQuery(id+"F1.opExtrude","SWEPT_FACE",FACE,{"disambiguationData":[OSD([subQ0,sQuery(id+"F0.wireOp",EDGE,"E15")])]}),makeQuery(id+"F2.opExtrude","SWEPT_FACE",FACE,{"disambiguationData":[OSD([subQ0])]})]}),makeQuery(id+"F8.opExtrude","SWEPT_FACE",FACE,{"disambiguationData":[OSD([sQuery(id+"F7.wireOp",EDGE,"E38")])]})]});}
            chamfer(context, id + "F21", {"entities" : qUnion([Q0, Q1, Q2, Q3, Q4, Q5, Q6, Q7, Q8, Q9, Q10, Q11, Q12, Q13]), "width" : 0.5 * mm, "tangentPropagation" : true});
        }
        {
            var Q0;
            {var subQ0=sQuery(id+"F0.wireOp",EDGE,"E4");var subQ1=sQuery(id+"F0.wireOp",EDGE,"E2.right");Q0=makeQuery(id+"F14.boolean.opBoolean","SPLIT",EDGE,{"disambiguationData":[TD([makeQuery(id+"F1.opExtrude","SWEPT_FACE",FACE,{"disambiguationData":[OSD([subQ1])]})])],"derivedFrom":makeQuery(id+"F2.opExtrude","CAP_EDGE",EDGE,{"disambiguationData":[OSD([subQ0])],"isStart":false})});}
            var Q1;
            {var subQ0=sQuery(id+"F0.wireOp",EDGE,"E4");var subQ1=sQuery(id+"F0.wireOp",EDGE,"E1");Q1=makeQuery(id+"F14.boolean.opBoolean","SPLIT",EDGE,{"disambiguationData":[TD([makeQuery(id+"F1.opExtrude","SWEPT_FACE",FACE,{"disambiguationData":[OSD([subQ1])]})])],"derivedFrom":makeQuery(id+"F2.opExtrude","CAP_EDGE",EDGE,{"disambiguationData":[OSD([subQ0])],"isStart":false})});}
            var Q2;
            Q2=makeQuery(id+"F14.boolean.opBoolean","COPY",EDGE,{"derivedFrom":makeQuery(id+"F14.opExtrude","SWEPT_EDGE",EDGE,{"disambiguationData":[OSD([sQuery(id+"F0.wireOp",EDGE,"E4"),sQuery(id+"F5.wireOp",EDGE,"E37.top"),sQuery(id+"F5.wireOp",EDGE,"E37.left")])]})});
            var Q3;
            Q3=makeQuery(id+"F14.boolean.opBoolean","COPY",EDGE,{"derivedFrom":makeQuery(id+"F14.opExtrude","CAP_EDGE",EDGE,{"disambiguationData":[OSD([sQuery(id+"F5.wireOp",EDGE,"E37.top")])],"isStart":false})});
            var Q4;
            {var subQ0=sQuery(id+"F0.wireOp",EDGE,"E4");var subQ1=sQuery(id+"F0.wireOp",EDGE,"E2.right");Q4=makeQuery(id+"F14.boolean.opBoolean","SPLIT",EDGE,{"disambiguationData":[TD([makeQuery(id+"F2.opExtrude","SWEPT_FACE",FACE,{"disambiguationData":[OSD([subQ1])]})])],"derivedFrom":makeQuery(id+"F2.opExtrude","CAP_EDGE",EDGE,{"disambiguationData":[OSD([subQ0])],"isStart":false})});}
            var Q5;
            Q5=makeQuery(id+"F14.boolean.opBoolean","COPY",EDGE,{"derivedFrom":makeQuery(id+"F14.opExtrude","CAP_EDGE",EDGE,{"disambiguationData":[OSD([sQuery(id+"F5.wireOp",EDGE,"E37.left")])],"isStart":true})});
            var Q6;
            Q6=makeQuery(id+"F14.boolean.opBoolean","COPY",EDGE,{"derivedFrom":makeQuery(id+"F14.opExtrude","CAP_EDGE",EDGE,{"disambiguationData":[OSD([sQuery(id+"F5.wireOp",EDGE,"E37.right")])],"isStart":true})});
            var Q7;
            Q7=makeQuery(id+"F14.boolean.opBoolean","COPY",EDGE,{"derivedFrom":makeQuery(id+"F14.opExtrude","SWEPT_EDGE",EDGE,{"disambiguationData":[OSD([sQuery(id+"F0.wireOp",EDGE,"E4"),sQuery(id+"F5.wireOp",EDGE,"E37.top"),sQuery(id+"F5.wireOp",EDGE,"E37.right")])]})});
            fillet(context, id + "F22", {"entities" : qUnion([Q0, Q1, Q2, Q3, Q4, Q5, Q6, Q7]), "tangentPropagation" : true, "radius" : 2.3 * mm, "defaultsChanged" : true, "vertexSettings" : [], "allowEdgeOverflow" : false});
        }
        {
            var Q0;
            Q0=makeQuery(id+"F6.opExtrude","CAP_EDGE",EDGE,{"disambiguationData":[OSD([sQuery(id+"F5.wireOp",EDGE,"E36.left")])],"isStart":true});
            var Q1;
            Q1=makeQuery(id+"F6.opExtrude","CAP_EDGE",EDGE,{"disambiguationData":[OSD([sQuery(id+"F5.wireOp",EDGE,"E34.right")])],"isStart":true});
            var Q2;
            Q2=makeQuery(id+"F6.opExtrude","CAP_EDGE",EDGE,{"disambiguationData":[OSD([sQuery(id+"F5.wireOp",EDGE,"E34.right")])],"isStart":false});
            var Q3;
            Q3=makeQuery(id+"F6.opExtrude","CAP_EDGE",EDGE,{"disambiguationData":[OSD([sQuery(id+"F5.wireOp",EDGE,"E34.left")])],"isStart":false});
            var Q4;
            Q4=makeQuery(id+"F6.opExtrude","CAP_EDGE",EDGE,{"disambiguationData":[OSD([sQuery(id+"F5.wireOp",EDGE,"E36.right")])],"isStart":false});
            var Q5;
            Q5=makeQuery(id+"F6.opExtrude","CAP_EDGE",EDGE,{"disambiguationData":[OSD([sQuery(id+"F5.wireOp",EDGE,"E36.left")])],"isStart":false});
            var Q6;
            Q6=makeQuery(id+"F6.opExtrude","CAP_EDGE",EDGE,{"disambiguationData":[OSD([sQuery(id+"F5.wireOp",EDGE,"E36.right")])],"isStart":true});
            fillet(context, id + "F23", {"entities" : qUnion([Q0, Q1, Q2, Q3, Q4, Q5, Q6]), "tangentPropagation" : true, "radius" : 7.5 * mm, "defaultsChanged" : false, "vertexSettings" : [], "allowEdgeOverflow" : false});
        }
    });
